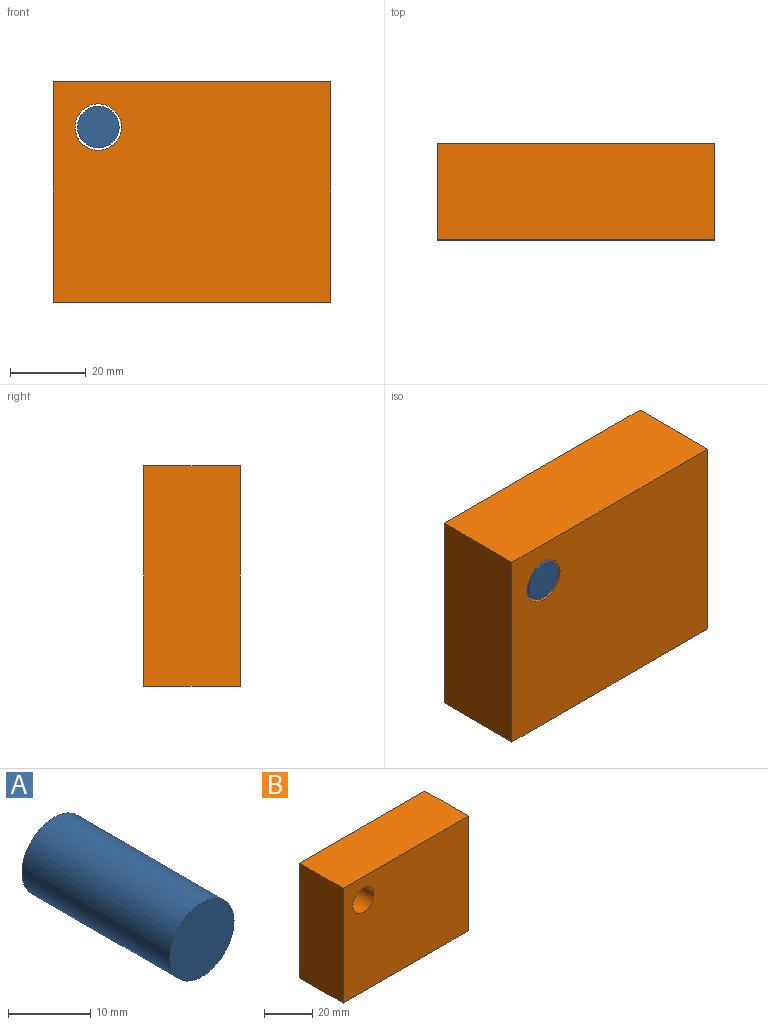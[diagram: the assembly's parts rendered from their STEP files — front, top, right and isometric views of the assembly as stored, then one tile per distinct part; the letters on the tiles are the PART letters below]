
ASSEMBLY  parts=2 mates=1
PART A: 3 faces, bbox 11x25.4x11 mm
  f0: cylinder r=5.51mm len=25.4mm, axis (0,1,0), area 878.9mm2, adj f1,f2
  f1: plane 11.01x11.01mm, normal (0,-1,0), area 95.3mm2, adj f0
  f2: plane 11.01x11.01mm, normal (0,1,0), area 95.3mm2, adj f0
PART B: 7 faces, bbox 73.3x25.4x58.2 mm
  f0: plane 73.32x25.4mm, normal (0,0,1), area 1862.4mm2, adj f1,f4,f5,f6
  f1: plane 58.21x25.4mm, normal (-1,0,0), area 1478.6mm2, adj f0,f2,f5,f6
  f2: plane 73.32x25.4mm, normal (0,0,-1), area 1862.4mm2, adj f1,f4,f5,f6
  f3: cylinder r=6.13mm len=25.4mm, axis (0,1,0), area 978.6mm2, adj f5,f6
  f4: plane 58.21x25.4mm, normal (1,0,0), area 1478.6mm2, adj f0,f2,f5,f6
  f5: plane 73.32x58.21mm, normal (0,-1,0), area 4150.1mm2, adj f0,f1,f2,f3,f4
  f6: plane 73.32x58.21mm, normal (0,1,0), area 4150.1mm2, adj f0,f1,f2,f3,f4
PLACE A t=(-148.69,-4.23,1.8)mm
PLACE B t=(-11.35,-4.23,0.31)mm
MATE fastened A.f0 <-> B.f3  axis (0,-1,0) through (-55.79,-29.63,18.62)mm
